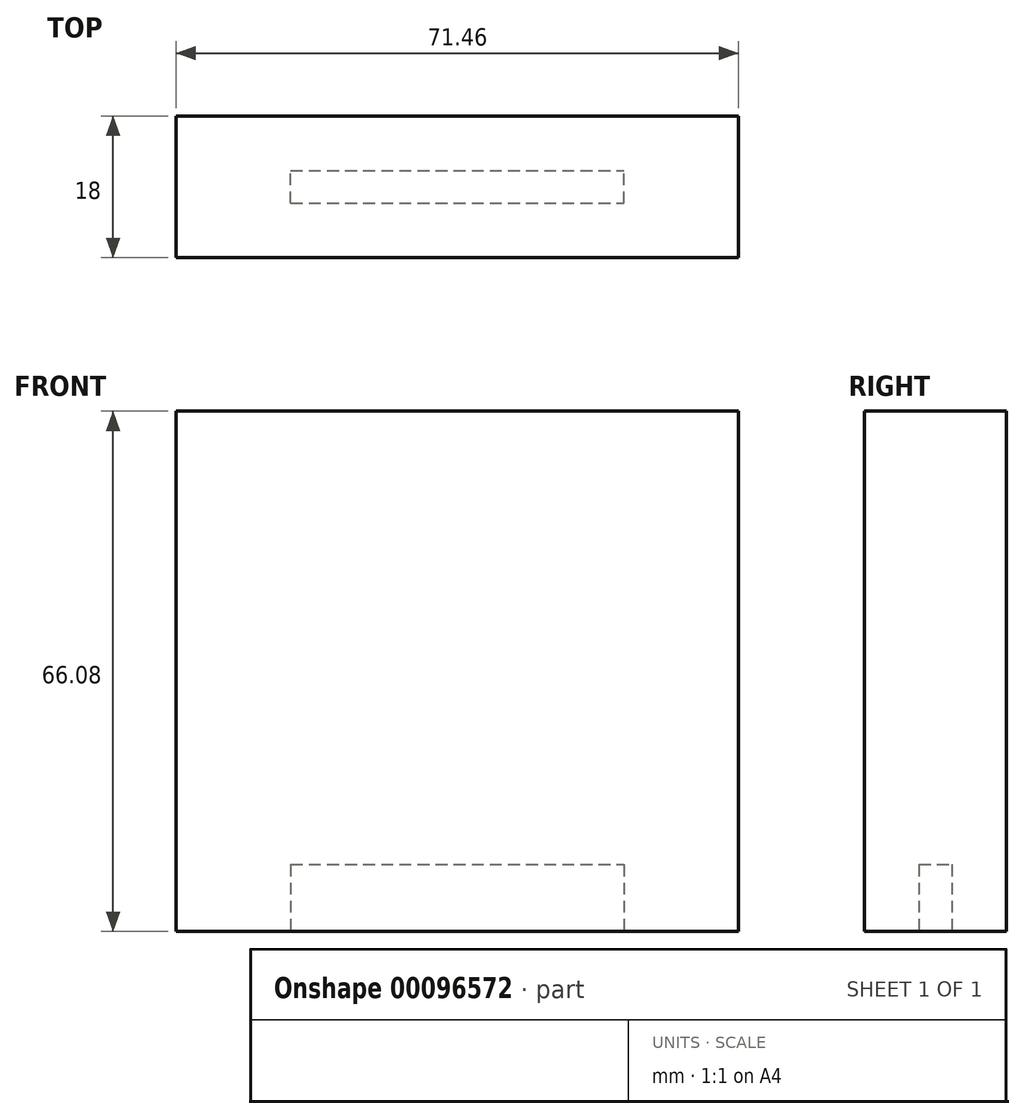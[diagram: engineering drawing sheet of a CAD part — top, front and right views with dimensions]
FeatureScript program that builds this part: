
annotation { "Feature Type Name" : "Feature", "Feature Type Description" : "" }
export const myFeature = defineFeature(function(context is Context, id is Id, definition is map)
    precondition{}
    {
        {
            var Q0;
            Q0=qCreatedBy(makeId("Front.planeOp"),FACE);
            var sketch = newSketch(context, id + "F0", { "sketchPlane" : qUnion([Q0])});
            skLineSegment(sketch, "E0.bottom", {"start": v(-35.73, 33.04) * mm, "end": v(35.73, 33.04) * mm});
            skLineSegment(sketch, "E0.top", {"start": v(-35.73, -33.04) * mm, "end": v(35.73, -33.04) * mm});
            skLineSegment(sketch, "E0.left", {"start": v(-35.73, 33.04) * mm, "end": v(-35.73, -33.04) * mm});
            skLineSegment(sketch, "E0.right", {"start": v(35.73, 33.04) * mm, "end": v(35.73, -33.04) * mm});
            skPoint(sketch, "E0.middle", {"position": v(0, 0) * mm});
            skSolve(sketch);
        }
        {
            var Q0;
            Q0=makeQuery(id+"F0.imprint","IMPRINT",FACE,{"disambiguationData":[TD([[makeQuery(id+"F0.imprint","IMPRINT",EDGE,{"derivedFrom":sQuery(id+"F0.wireOp",EDGE,"E0.bottom")}),-1.0]])]});
            extrude(context, id + "F1", {"entities" : qUnion([Q0]), "depth" : 18 * mm, "symmetric" : true});
        }
        {
            var Q0;
            Q0=makeQuery(id+"F1.opExtrude","SWEPT_FACE",FACE,{"disambiguationData":[OSD([sQuery(id+"F0.wireOp",EDGE,"E0.top")])]});
            var sketch = newSketch(context, id + "F2", { "sketchPlane" : qUnion([Q0])});
            skLineSegment(sketch, "E1.bottom", {"start": v(-21.15, 2.08) * mm, "end": v(21.15, 2.08) * mm});
            skLineSegment(sketch, "E1.top", {"start": v(-21.15, -2.08) * mm, "end": v(21.15, -2.08) * mm});
            skLineSegment(sketch, "E1.left", {"start": v(-21.15, 2.08) * mm, "end": v(-21.15, -2.08) * mm});
            skLineSegment(sketch, "E1.right", {"start": v(21.15, 2.08) * mm, "end": v(21.15, -2.08) * mm});
            skPoint(sketch, "E1.middle", {"position": v(0, 0) * mm});
            skSolve(sketch);
        }
        {
            var Q0;
            Q0=makeQuery(id+"F2.imprint","IMPRINT",FACE,{"disambiguationData":[TD([[makeQuery(id+"F2.imprint","IMPRINT",EDGE,{"derivedFrom":sQuery(id+"F2.wireOp",EDGE,"E1.bottom")}),-1.0]])]});
            extrude(context, id + "F3", {"entities" : qUnion([Q0]), "operationType" : NewBodyOperationType.REMOVE, "oppositeDirection" : true, "depth" : 8.5 * mm});
        }
    });
